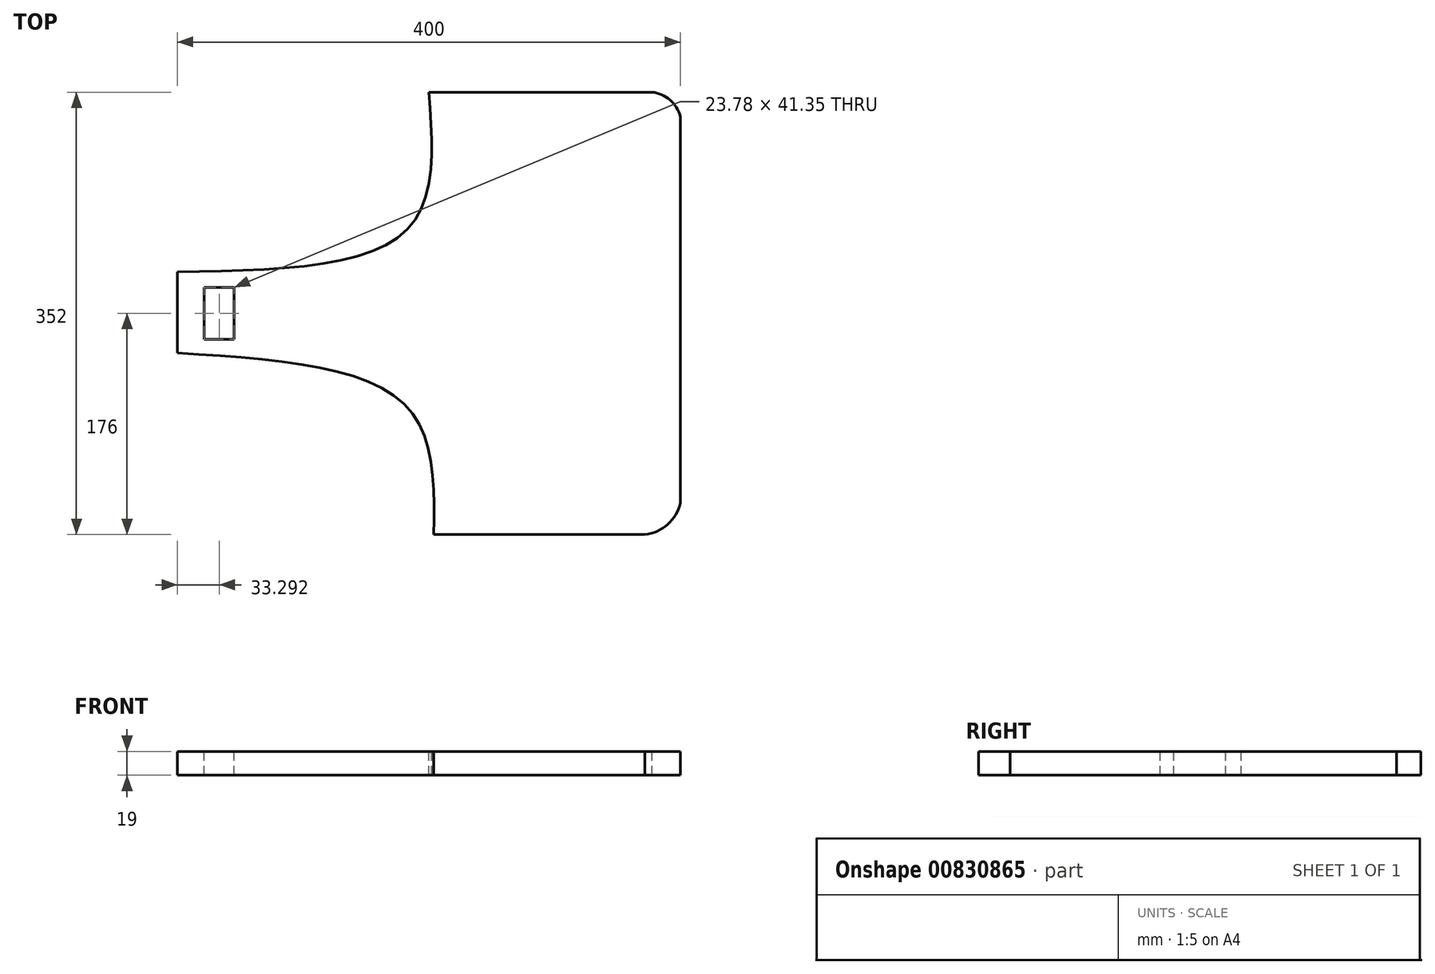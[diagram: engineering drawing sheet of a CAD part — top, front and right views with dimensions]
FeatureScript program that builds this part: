
annotation { "Feature Type Name" : "Feature", "Feature Type Description" : "" }
export const myFeature = defineFeature(function(context is Context, id is Id, definition is map)
    precondition{}
    {
        {
            var Q0;
            Q0=qCreatedBy(makeId("Top.planeOp"),FACE);
            var sketch = newSketch(context, id + "F0", { "sketchPlane" : qUnion([Q0])});
            skLineSegment(sketch, "E0.bottom", {"start": v(200, -176) * mm, "end": v(-200, -176) * mm});
            skLineSegment(sketch, "E0.top", {"start": v(200, 176) * mm, "end": v(-200, 176) * mm});
            skLineSegment(sketch, "E0.left", {"start": v(200, -176) * mm, "end": v(200, 176) * mm});
            skLineSegment(sketch, "E0.right", {"start": v(-200, -176) * mm, "end": v(-200, 176) * mm});
            skPoint(sketch, "E0.middle", {"position": v(0, 0) * mm});
            skSolve(sketch);
        }
        {
            var Q0;
            Q0=makeQuery(id+"F0.imprint","IMPRINT",FACE,{"disambiguationData":[TD([[makeQuery(id+"F0.imprint","IMPRINT",EDGE,{"derivedFrom":sQuery(id+"F0.wireOp",EDGE,"E0.bottom")}),-1.0]])]});
            extrude(context, id + "F1", {"entities" : qUnion([Q0]), "depth" : 19 * mm, "offsetDistance" : 25 * mm});
        }
        {
            var Q0;
            Q0=makeQuery(id+"F1.opExtrude","CAP_FACE",FACE,{"disambiguationData":[OSD([sQuery(id+"F0.wireOp",EDGE,"E0.bottom"),sQuery(id+"F0.wireOp",EDGE,"E0.top"),sQuery(id+"F0.wireOp",EDGE,"E0.left"),sQuery(id+"F0.wireOp",EDGE,"E0.right")])],"isStart":false});
            var sketch = newSketch(context, id + "F2", { "sketchPlane" : qUnion([Q0])});
            skFitSpline(sketch, "E1", {"points": [v(-200, -31.53) * mm, v(-18.87, -72.89) * mm, v(3.88, -176) * mm], "startDerivative": vector(393.17, -24.82) * mm, "endDerivative": vector(-3.99, -275.86) * mm});
            skFitSpline(sketch, "E2", {"points": [v(-200, 33.08) * mm, v(-17.32, 66.68) * mm, v(0, 176) * mm], "startDerivative": vector(403.82, 5.53) * mm, "endDerivative": vector(-22.1, 292.62) * mm});
            skArc(sketch, "E3", {"start": v(200, 160.76) * mm, "mid": v(187.77, 171.76) * mm, "end": v(171.88, 176) * mm});
            skArc(sketch, "E4", {"start": v(171.88, -176) * mm, "mid": v(189.88, -167.9) * mm, "end": v(200, -150.94) * mm});
            skSolve(sketch);
        }
        {
            var Q0;
            {var subQ0=sQuery(id+"F2.wireOp",EDGE,"E1");Q0=makeQuery(id+"F2.imprint","IMPRINT",FACE,{"disambiguationData":[TD([[makeQuery(id+"F2.imprint","IMPRINT",EDGE,{"derivedFrom":subQ0}),-1.0]])]});}
            var Q1;
            {var subQ0=sQuery(id+"F2.wireOp",EDGE,"E2");Q1=makeQuery(id+"F2.imprint","IMPRINT",FACE,{"disambiguationData":[TD([[makeQuery(id+"F2.imprint","IMPRINT",EDGE,{"derivedFrom":subQ0}),1.0]])]});}
            var Q2;
            {var subQ0=sQuery(id+"F2.wireOp",EDGE,"E4");Q2=makeQuery(id+"F2.imprint","IMPRINT",FACE,{"disambiguationData":[TD([[makeQuery(id+"F2.imprint","IMPRINT",EDGE,{"derivedFrom":subQ0}),-1.0]])]});}
            extrude(context, id + "F3", {"entities" : qUnion([Q0, Q1, Q2]), "operationType" : NewBodyOperationType.REMOVE, "endBound" : BoundingType.THROUGH_ALL, "oppositeDirection" : true, "depth" : 25 * mm, "offsetDistance" : 25 * mm});
        }
        {
            var Q0;
            Q0=makeQuery(id+"F1.opExtrude","CAP_FACE",FACE,{"disambiguationData":[OSD([sQuery(id+"F0.wireOp",EDGE,"E0.bottom"),sQuery(id+"F0.wireOp",EDGE,"E0.top"),sQuery(id+"F0.wireOp",EDGE,"E0.left"),sQuery(id+"F0.wireOp",EDGE,"E0.right")])],"isStart":false});
            var sketch = newSketch(context, id + "F4", { "sketchPlane" : qUnion([Q0])});
            skArc(sketch, "E5", {"start": v(200, 156.63) * mm, "mid": v(189.53, 171.52) * mm, "end": v(171.88, 176) * mm});
            skSolve(sketch);
        }
        {
            var Q0;
            {var subQ0=sQuery(id+"F4.wireOp",EDGE,"E5");var subQ1=makeQuery(id+"F1.opExtrude","CAP_EDGE",EDGE,{"disambiguationData":[OSD([sQuery(id+"F0.wireOp",EDGE,"E0.left")])],"isStart":false});var subQ2=makeQuery(id+"F4.imprint","INTERSECT",VERTEX,{"derivedFrom":[subQ1,subQ0]});Q0=makeQuery(id+"F4.imprint","IMPRINT",FACE,{"disambiguationData":[TD([[makeQuery(id+"F4.imprint","IMPRINT",EDGE,{"disambiguationData":[TD([[subQ2,-1.0]])],"derivedFrom":subQ0}),-1.0]])]});}
            extrude(context, id + "F5", {"entities" : qUnion([Q0]), "operationType" : NewBodyOperationType.REMOVE, "endBound" : BoundingType.THROUGH_ALL, "oppositeDirection" : true, "depth" : 25 * mm, "offsetDistance" : 25 * mm});
        }
        {
            var Q0;
            Q0=makeQuery(id+"F1.opExtrude","CAP_FACE",FACE,{"disambiguationData":[OSD([sQuery(id+"F0.wireOp",EDGE,"E0.bottom"),sQuery(id+"F0.wireOp",EDGE,"E0.top"),sQuery(id+"F0.wireOp",EDGE,"E0.left"),sQuery(id+"F0.wireOp",EDGE,"E0.right")])],"isStart":false});
            var sketch = newSketch(context, id + "F6", { "sketchPlane" : qUnion([Q0])});
            skLineSegment(sketch, "E6.bottom", {"start": v(-154.82, -20.68) * mm, "end": v(-178.6, -20.68) * mm});
            skLineSegment(sketch, "E6.top", {"start": v(-154.82, 20.68) * mm, "end": v(-178.6, 20.68) * mm});
            skLineSegment(sketch, "E6.left", {"start": v(-154.82, -20.68) * mm, "end": v(-154.82, 20.68) * mm});
            skLineSegment(sketch, "E6.right", {"start": v(-178.6, -20.68) * mm, "end": v(-178.6, 20.68) * mm});
            skPoint(sketch, "E6.middle", {"position": v(-166.7, 0) * mm});
            skSolve(sketch);
        }
        {
            var Q0;
            Q0=makeQuery(id+"F6.imprint","IMPRINT",FACE,{"disambiguationData":[TD([[makeQuery(id+"F6.imprint","IMPRINT",EDGE,{"derivedFrom":sQuery(id+"F6.wireOp",EDGE,"E6.bottom")}),-1.0]])]});
            extrude(context, id + "F7", {"entities" : qUnion([Q0]), "operationType" : NewBodyOperationType.REMOVE, "endBound" : BoundingType.THROUGH_ALL, "oppositeDirection" : true, "depth" : 25 * mm, "offsetDistance" : 25 * mm});
        }
    });
